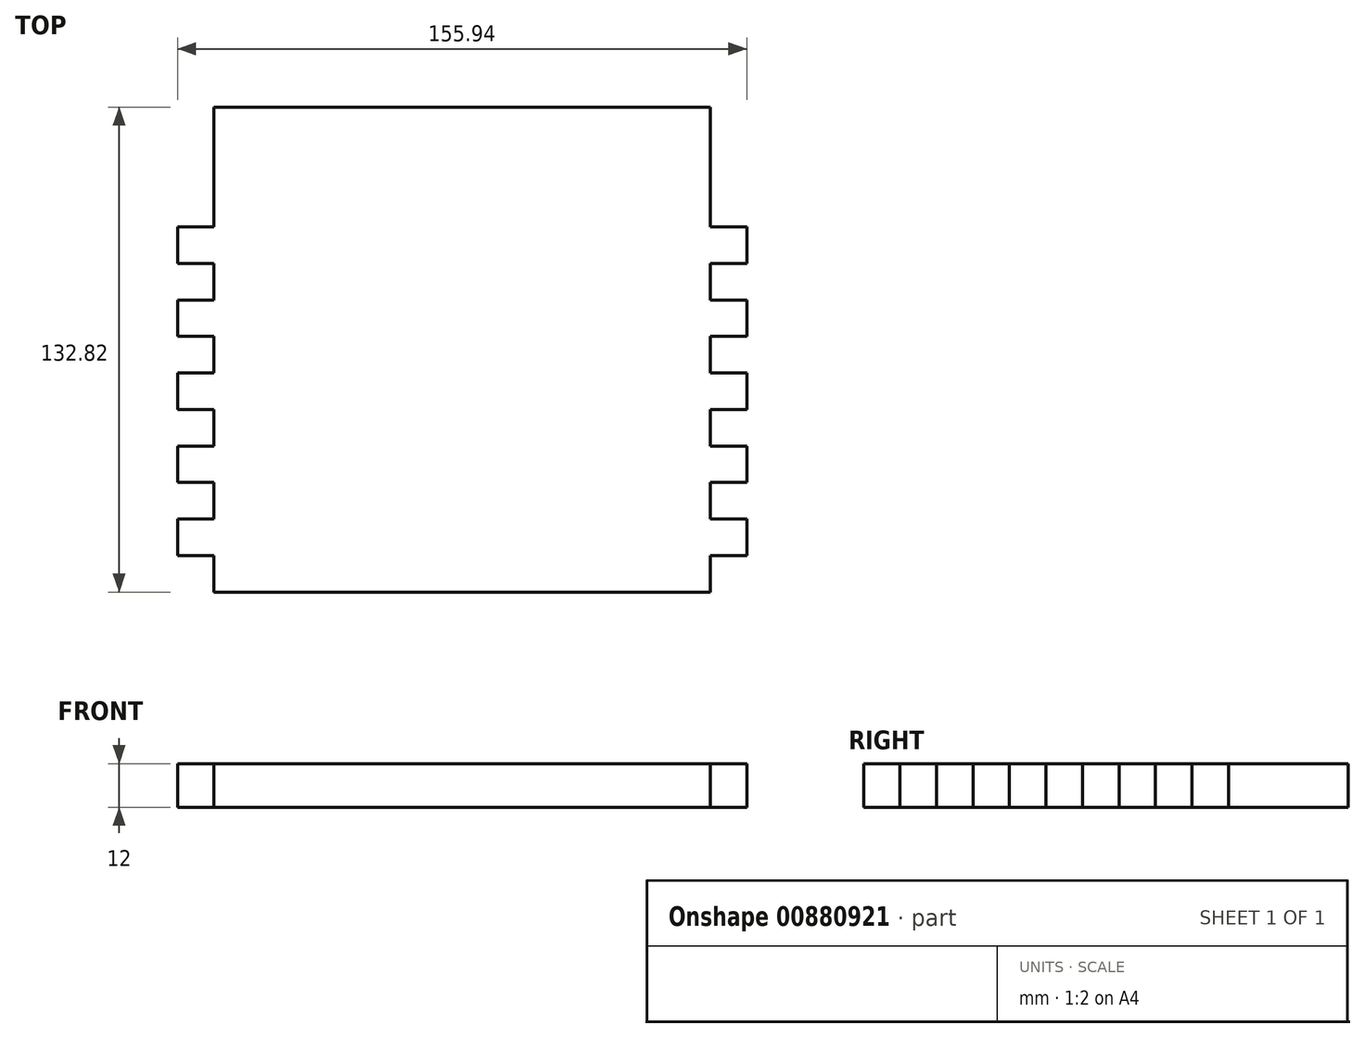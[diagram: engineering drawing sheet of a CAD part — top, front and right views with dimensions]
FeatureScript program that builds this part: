
annotation { "Feature Type Name" : "Feature", "Feature Type Description" : "" }
export const myFeature = defineFeature(function(context is Context, id is Id, definition is map)
    precondition{}
    {
        {
            var Q0;
            Q0=qCreatedBy(makeId("Top.planeOp"),FACE);
            var sketch = newSketch(context, id + "F0", { "sketchPlane" : qUnion([Q0])});
            skLineSegment(sketch, "E0.bottom", {"start": v(67.97, 66.4) * mm, "end": v(0, 66.4) * mm});
            skLineSegment(sketch, "E0.top", {"start": v(67.97, -66.4) * mm, "end": v(0, -66.4) * mm});
            skLineSegment(sketch, "E0.left", {"start": v(77.97, 33.6) * mm, "end": v(77.97, 23.6) * mm});
            skPoint(sketch, "E0.middle", {"position": v(0, 0) * mm});
            skLineSegment(sketch, "E1", {"start": v(67.97, -66.4) * mm, "end": v(67.97, -56.4) * mm});
            skLineSegment(sketch, "E2", {"start": v(67.97, -56.4) * mm, "end": v(77.97, -56.4) * mm});
            skLineSegment(sketch, "E3", {"start": v(67.97, -46.4) * mm, "end": v(77.97, -46.4) * mm});
            skLineSegment(sketch, "E4", {"start": v(67.97, -36.4) * mm, "end": v(77.97, -36.4) * mm});
            skLineSegment(sketch, "E5", {"start": v(67.97, -26.4) * mm, "end": v(77.97, -26.4) * mm});
            skLineSegment(sketch, "E6", {"start": v(67.97, -16.4) * mm, "end": v(77.97, -16.4) * mm});
            skLineSegment(sketch, "E7", {"start": v(67.97, -6.4) * mm, "end": v(77.97, -6.4) * mm});
            skLineSegment(sketch, "E8", {"start": v(67.97, 3.6) * mm, "end": v(77.97, 3.6) * mm});
            skLineSegment(sketch, "E9", {"start": v(67.97, 13.6) * mm, "end": v(77.97, 13.6) * mm});
            skLineSegment(sketch, "E10", {"start": v(67.97, 23.6) * mm, "end": v(77.97, 23.6) * mm});
            skLineSegment(sketch, "E11", {"start": v(67.97, 33.6) * mm, "end": v(77.97, 33.6) * mm});
            skLineSegment(sketch, "E12.trimOffspring", {"start": v(67.97, 33.6) * mm, "end": v(67.97, 66.4) * mm});
            skLineSegment(sketch, "E13.trimOffspring", {"start": v(77.97, 13.6) * mm, "end": v(77.97, 3.6) * mm});
            skLineSegment(sketch, "E14.trimOffspring", {"start": v(67.97, 13.6) * mm, "end": v(67.97, 23.6) * mm});
            skLineSegment(sketch, "E15.trimOffspring", {"start": v(77.97, -6.4) * mm, "end": v(77.97, -16.4) * mm});
            skLineSegment(sketch, "E16.trimOffspring", {"start": v(67.97, -6.4) * mm, "end": v(67.97, 3.6) * mm});
            skLineSegment(sketch, "E17.trimOffspring", {"start": v(77.97, -26.4) * mm, "end": v(77.97, -36.4) * mm});
            skLineSegment(sketch, "E18.trimOffspring", {"start": v(67.97, -26.4) * mm, "end": v(67.97, -16.4) * mm});
            skLineSegment(sketch, "E19.trimOffspring", {"start": v(77.97, -46.4) * mm, "end": v(77.97, -56.4) * mm});
            skLineSegment(sketch, "E20.trimOffspring", {"start": v(67.97, -46.4) * mm, "end": v(67.97, -36.4) * mm});
            skPoint(sketch, "E21.orphan", {"position": v(77.97, 66.4) * mm});
            skLineSegment(sketch, "E22", {"start": v(0, 66.4) * mm, "end": v(0, -66.4) * mm});
            skPoint(sketch, "E0.right.start.orphan", {"position": v(-77.97, 66.4) * mm});
            skPoint(sketch, "E23.orphan", {"position": v(-77.97, -66.4) * mm});
            skLineSegment(sketch, "E24.MirrorCS", {"start": v(-67.97, -56.4) * mm, "end": v(-77.97, -56.4) * mm});
            skLineSegment(sketch, "E25.MirrorCS", {"start": v(-67.97, -6.4) * mm, "end": v(-77.97, -6.4) * mm});
            skLineSegment(sketch, "E26.MirrorCS", {"start": v(-67.97, 23.6) * mm, "end": v(-77.97, 23.6) * mm});
            skLineSegment(sketch, "E27.MirrorCS", {"start": v(-67.97, 13.6) * mm, "end": v(-77.97, 13.6) * mm});
            skLineSegment(sketch, "E28.MirrorCS", {"start": v(-67.97, -36.4) * mm, "end": v(-77.97, -36.4) * mm});
            skLineSegment(sketch, "E29.MirrorCS", {"start": v(-67.97, 3.6) * mm, "end": v(-77.97, 3.6) * mm});
            skLineSegment(sketch, "E30.MirrorCS", {"start": v(-67.97, 33.6) * mm, "end": v(-77.97, 33.6) * mm});
            skLineSegment(sketch, "E31.MirrorCS", {"start": v(-67.97, -26.4) * mm, "end": v(-77.97, -26.4) * mm});
            skLineSegment(sketch, "E32.MirrorCS", {"start": v(-67.97, -46.4) * mm, "end": v(-77.97, -46.4) * mm});
            skLineSegment(sketch, "E33.MirrorCS", {"start": v(-67.97, -46.4) * mm, "end": v(-67.97, -36.4) * mm});
            skLineSegment(sketch, "E34.MirrorCS", {"start": v(-67.97, -66.4) * mm, "end": v(0, -66.4) * mm});
            skLineSegment(sketch, "E35.MirrorCS", {"start": v(-67.97, -26.4) * mm, "end": v(-67.97, -16.4) * mm});
            skLineSegment(sketch, "E36.MirrorCS", {"start": v(-77.97, 33.6) * mm, "end": v(-77.97, 23.6) * mm});
            skLineSegment(sketch, "E37.MirrorCS", {"start": v(-77.97, -6.4) * mm, "end": v(-77.97, -16.4) * mm});
            skLineSegment(sketch, "E38.MirrorCS", {"start": v(-67.97, -16.4) * mm, "end": v(-77.97, -16.4) * mm});
            skLineSegment(sketch, "E39.MirrorCS", {"start": v(-77.97, -46.4) * mm, "end": v(-77.97, -56.4) * mm});
            skLineSegment(sketch, "E40.MirrorCS", {"start": v(-67.97, 13.6) * mm, "end": v(-67.97, 23.6) * mm});
            skLineSegment(sketch, "E41.MirrorCS", {"start": v(-77.97, 13.6) * mm, "end": v(-77.97, 3.6) * mm});
            skLineSegment(sketch, "E42.MirrorCS", {"start": v(-67.97, 66.4) * mm, "end": v(0, 66.4) * mm});
            skLineSegment(sketch, "E43.MirrorCS", {"start": v(-67.97, -66.4) * mm, "end": v(-67.97, -56.4) * mm});
            skLineSegment(sketch, "E44.MirrorCS", {"start": v(-67.97, -6.4) * mm, "end": v(-67.97, 3.6) * mm});
            skLineSegment(sketch, "E45.MirrorCS", {"start": v(-67.97, 33.6) * mm, "end": v(-67.97, 66.4) * mm});
            skLineSegment(sketch, "E46.MirrorCS", {"start": v(-77.97, -26.4) * mm, "end": v(-77.97, -36.4) * mm});
            skPoint(sketch, "E47.orphan", {"position": v(77.97, -66.4) * mm});
            skSolve(sketch);
        }
        {
            var Q0;
            Q0=makeQuery(id+"F0.imprint","IMPRINT",FACE,{"disambiguationData":[TD([[makeQuery(id+"F0.imprint","IMPRINT",EDGE,{"derivedFrom":sQuery(id+"F0.wireOp",EDGE,"E22")}),-1.0]])]});
            var Q1;
            Q1=makeQuery(id+"F0.imprint","IMPRINT",FACE,{"disambiguationData":[TD([[makeQuery(id+"F0.imprint","IMPRINT",EDGE,{"derivedFrom":sQuery(id+"F0.wireOp",EDGE,"E0.bottom")}),1.0]])]});
            extrude(context, id + "F1", {"entities" : qUnion([Q0, Q1]), "depth" : 12 * mm, "offsetDistance" : 25 * mm});
        }
    });
